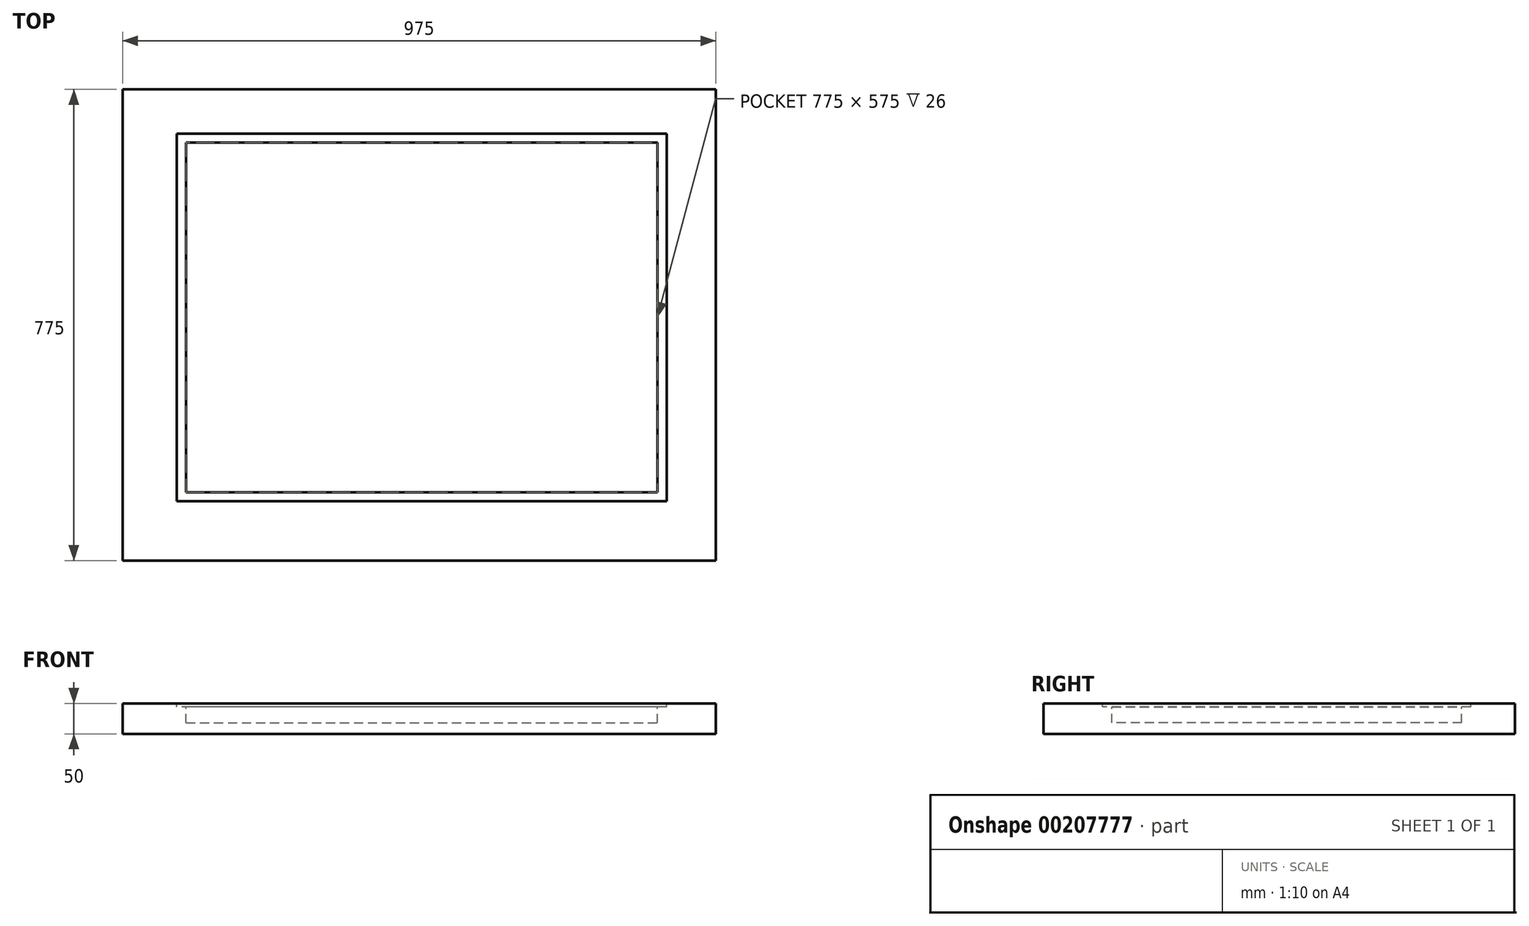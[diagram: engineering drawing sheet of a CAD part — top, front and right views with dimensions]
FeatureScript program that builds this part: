
annotation { "Feature Type Name" : "Feature", "Feature Type Description" : "" }
export const myFeature = defineFeature(function(context is Context, id is Id, definition is map)
    precondition{}
    {
        {
            var Q0;
            Q0=qCreatedBy(makeId("Top.planeOp"),FACE);
            var sketch = newSketch(context, id + "F0", { "sketchPlane" : qUnion([Q0])});
            skLineSegment(sketch, "E0.bottom", {"start": v(0, 0) * mm, "end": v(975, 0) * mm});
            skLineSegment(sketch, "E0.top", {"start": v(0, 775) * mm, "end": v(975, 775) * mm});
            skLineSegment(sketch, "E0.left", {"start": v(0, 0) * mm, "end": v(0, 775) * mm});
            skLineSegment(sketch, "E0.right", {"start": v(975, 0) * mm, "end": v(975, 775) * mm});
            skSolve(sketch);
        }
        {
            var Q0;
            Q0=makeQuery(id+"F0.imprint","IMPRINT",FACE,{"disambiguationData":[TD([[makeQuery(id+"F0.imprint","IMPRINT",EDGE,{"derivedFrom":sQuery(id+"F0.wireOp",EDGE,"E0.bottom")}),1.0]])]});
            extrude(context, id + "F1", {"entities" : qUnion([Q0]), "depth" : 50 * mm});
        }
        {
            var Q0;
            Q0=makeQuery(id+"F1.opExtrude","CAP_FACE",FACE,{"disambiguationData":[OSD([sQuery(id+"F0.wireOp",EDGE,"E0.bottom"),sQuery(id+"F0.wireOp",EDGE,"E0.top"),sQuery(id+"F0.wireOp",EDGE,"E0.left"),sQuery(id+"F0.wireOp",EDGE,"E0.right")])],"isStart":false});
            var sketch = newSketch(context, id + "F2", { "sketchPlane" : qUnion([Q0])});
            skLineSegment(sketch, "E1.bottom", {"start": v(104.42, 687.44) * mm, "end": v(879.42, 687.44) * mm});
            skLineSegment(sketch, "E1.top", {"start": v(104.42, 112.44) * mm, "end": v(879.42, 112.44) * mm});
            skLineSegment(sketch, "E1.left", {"start": v(104.42, 687.44) * mm, "end": v(104.42, 112.44) * mm});
            skLineSegment(sketch, "E1.right", {"start": v(879.42, 687.44) * mm, "end": v(879.42, 112.44) * mm});
            skSolve(sketch);
        }
        {
            var Q0;
            Q0=makeQuery(id+"F2.imprint","IMPRINT",FACE,{"disambiguationData":[TD([[makeQuery(id+"F2.imprint","IMPRINT",EDGE,{"derivedFrom":sQuery(id+"F2.wireOp",EDGE,"E1.bottom")}),-1.0]])]});
            extrude(context, id + "F3", {"entities" : qUnion([Q0]), "operationType" : NewBodyOperationType.REMOVE, "oppositeDirection" : true, "depth" : 32 * mm});
        }
        {
            var Q0;
            Q0=makeQuery(id+"F1.opExtrude","CAP_FACE",FACE,{"disambiguationData":[OSD([sQuery(id+"F0.wireOp",EDGE,"E0.bottom"),sQuery(id+"F0.wireOp",EDGE,"E0.top"),sQuery(id+"F0.wireOp",EDGE,"E0.left"),sQuery(id+"F0.wireOp",EDGE,"E0.right")])],"isStart":false});
            var sketch = newSketch(context, id + "F4", { "sketchPlane" : qUnion([Q0])});
            skLineSegment(sketch, "E2.0", {"start": v(89.42, 702.44) * mm, "end": v(89.42, 97.44) * mm});
            skLineSegment(sketch, "E2.1", {"start": v(894.42, 702.44) * mm, "end": v(89.42, 702.44) * mm});
            skLineSegment(sketch, "E2.2", {"start": v(894.42, 97.44) * mm, "end": v(894.42, 702.44) * mm});
            skLineSegment(sketch, "E2.3", {"start": v(89.42, 97.44) * mm, "end": v(894.42, 97.44) * mm});
            skSolve(sketch);
        }
        {
            var Q0;
            Q0 = qSketchRegion(id + "F4", true);
            extrude(context, id + "F5", {"entities" : qUnion([Q0]), "operationType" : NewBodyOperationType.REMOVE, "oppositeDirection" : true, "depth" : 6 * mm});
        }
    });
